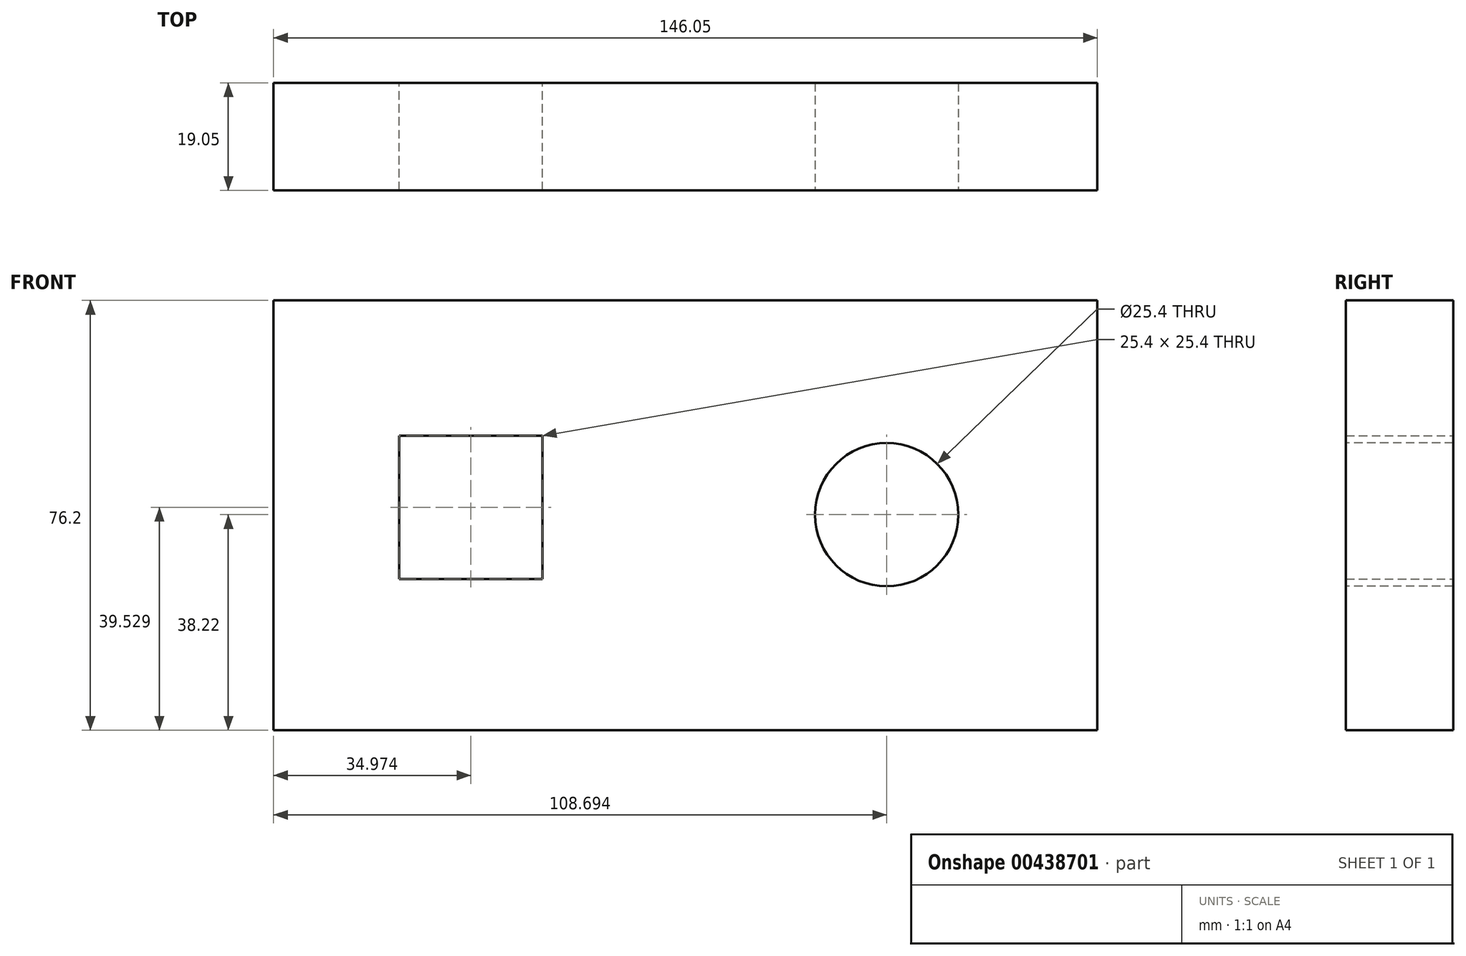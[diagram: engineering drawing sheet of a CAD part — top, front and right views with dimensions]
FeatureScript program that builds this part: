
annotation { "Feature Type Name" : "Feature", "Feature Type Description" : "" }
export const myFeature = defineFeature(function(context is Context, id is Id, definition is map)
    precondition{}
    {
        {
            var Q0;
            Q0=qCreatedBy(makeId("Front.planeOp"),FACE);
            var sketch = newSketch(context, id + "F0", { "sketchPlane" : qUnion([Q0])});
            skLineSegment(sketch, "E0", {"start": v(-72.58, -38.22) * mm, "end": v(73.47, -38.22) * mm});
            skLineSegment(sketch, "E1", {"start": v(-72.58, -38.22) * mm, "end": v(-72.58, 37.98) * mm});
            skLineSegment(sketch, "E2", {"start": v(73.47, -38.22) * mm, "end": v(73.47, 37.98) * mm});
            skLineSegment(sketch, "E3", {"start": v(73.47, 37.98) * mm, "end": v(-72.58, 37.98) * mm});
            skSolve(sketch);
        }
        {
            var Q0;
            Q0=makeQuery(id+"F0.imprint","IMPRINT",FACE,{"disambiguationData":[TD([[makeQuery(id+"F0.imprint","IMPRINT",EDGE,{"derivedFrom":sQuery(id+"F0.wireOp",EDGE,"E0")}),1.0]])]});
            extrude(context, id + "F1", {"entities" : qUnion([Q0]), "depth" : 19.05 * mm});
        }
        {
            var Q0;
            Q0=makeQuery(id+"F1.opExtrude","CAP_FACE",FACE,{"disambiguationData":[OSD([sQuery(id+"F0.wireOp",EDGE,"E0"),sQuery(id+"F0.wireOp",EDGE,"E1"),sQuery(id+"F0.wireOp",EDGE,"E2"),sQuery(id+"F0.wireOp",EDGE,"E3")])],"isStart":false});
            var sketch = newSketch(context, id + "F2", { "sketchPlane" : qUnion([Q0])});
            skCircle(sketch, "E4", {"center": v(36.11, 0) * mm, "radius": 12.7 * mm});
            skSolve(sketch);
        }
        {
            var Q0;
            Q0=makeQuery(id+"F2.imprint","IMPRINT",FACE,{"disambiguationData":[TD([[makeQuery(id+"F2.imprint","IMPRINT",EDGE,{"derivedFrom":sQuery(id+"F2.wireOp",EDGE,"E4")}),1.0]])]});
            extrude(context, id + "F3", {"entities" : qUnion([Q0]), "operationType" : NewBodyOperationType.REMOVE, "oppositeDirection" : true, "depth" : 19.05 * mm});
        }
        {
            var Q0;
            Q0=qCreatedBy(makeId("Front.planeOp"),FACE);
            var sketch = newSketch(context, id + "F4", { "sketchPlane" : qUnion([Q0])});
            skLineSegment(sketch, "E5", {"start": v(-50.93, -12.64) * mm, "end": v(-25.53, -12.64) * mm});
            skLineSegment(sketch, "E6", {"start": v(-25.53, -12.64) * mm, "end": v(-25.53, 12.76) * mm});
            skLineSegment(sketch, "E7", {"start": v(-25.53, 12.76) * mm, "end": v(-50.93, 12.76) * mm});
            skLineSegment(sketch, "E8", {"start": v(-50.93, 12.76) * mm, "end": v(-50.93, -12.64) * mm});
            skSolve(sketch);
        }
        {
            var Q0;
            Q0 = qSketchRegion(id + "F4", true);
            extrude(context, id + "F5", {"entities" : qUnion([Q0]), "operationType" : NewBodyOperationType.REMOVE, "oppositeDirection" : true, "depth" : 19.05 * mm});
        }
        {
            var Q0;
            Q0=qCreatedBy(makeId("Front.planeOp"),FACE);
            var sketch = newSketch(context, id + "F6", { "sketchPlane" : qUnion([Q0])});
            skLineSegment(sketch, "E9", {"start": v(-50.3, -11.4) * mm, "end": v(-24.9, -11.4) * mm});
            skLineSegment(sketch, "E10", {"start": v(-24.9, -11.4) * mm, "end": v(-24.9, 14) * mm});
            skLineSegment(sketch, "E11", {"start": v(-24.9, 14) * mm, "end": v(-50.3, 14) * mm});
            skLineSegment(sketch, "E12", {"start": v(-50.3, 14) * mm, "end": v(-50.3, -11.4) * mm});
            skSolve(sketch);
        }
        {
            var Q0;
            Q0=makeQuery(id+"F6.imprint","IMPRINT",FACE,{"disambiguationData":[TD([[makeQuery(id+"F6.imprint","IMPRINT",EDGE,{"derivedFrom":sQuery(id+"F6.wireOp",EDGE,"E9")}),1.0]])]});
            extrude(context, id + "F7", {"entities" : qUnion([Q0]), "operationType" : NewBodyOperationType.REMOVE, "depth" : 19.05 * mm});
        }
    });
